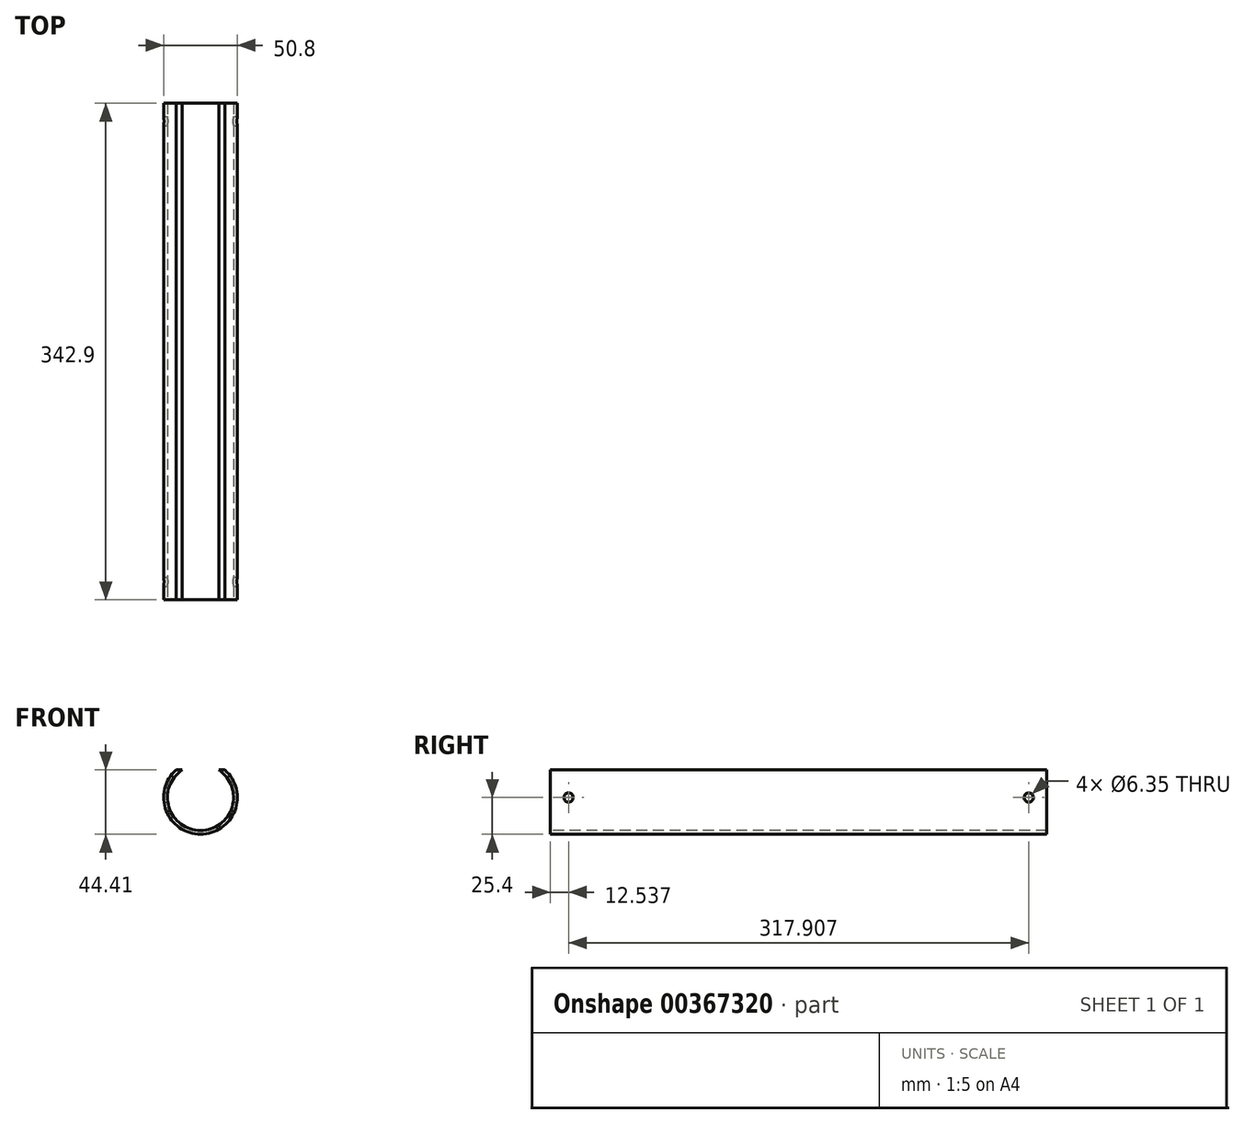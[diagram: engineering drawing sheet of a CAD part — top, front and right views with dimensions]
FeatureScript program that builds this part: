
annotation { "Feature Type Name" : "Feature", "Feature Type Description" : "" }
export const myFeature = defineFeature(function(context is Context, id is Id, definition is map)
    precondition{}
    {
        {
            var Q0;
            Q0=qCreatedBy(makeId("Front.planeOp"),FACE);
            var sketch = newSketch(context, id + "F0", { "sketchPlane" : qUnion([Q0])});
            skCircle(sketch, "E0", {"center": v(0, 0) * mm, "radius": 25.4 * mm});
            skSolve(sketch);
        }
        {
            var Q0;
            Q0 = qSketchRegion(id + "F0", true);
            extrude(context, id + "F1", {"entities" : qUnion([Q0]), "depth" : 342.9 * mm});
        }
        {
            var Q0;
            Q0=makeQuery(id+"F1.opExtrude","CAP_FACE",FACE,{"disambiguationData":[OSD([sQuery(id+"F0.wireOp",EDGE,"E0")])],"isStart":false});
            var sketch = newSketch(context, id + "F2", { "sketchPlane" : qUnion([Q0])});
            skCircle(sketch, "E1", {"center": v(0, 0) * mm, "radius": 22.86 * mm});
            skSolve(sketch);
        }
        {
            var Q0;
            Q0 = qSketchRegion(id + "F2", true);
            var Q1;
            Q1=makeQuery(id+"F1.opExtrude","CAP_FACE",FACE,{"disambiguationData":[OSD([sQuery(id+"F0.wireOp",EDGE,"E0")])],"isStart":true});
            extrude(context, id + "F3", {"entities" : qUnion([Q0]), "operationType" : NewBodyOperationType.REMOVE, "endBound" : BoundingType.UP_TO_SURFACE, "oppositeDirection" : true, "endBoundEntityFace" : qUnion([Q1]), "depth" : 25.4 * mm});
        }
        {
            var Q0;
            Q0=makeQuery(id+"F1.opExtrude","CAP_FACE",FACE,{"disambiguationData":[OSD([sQuery(id+"F0.wireOp",EDGE,"E0")])],"isStart":false});
            var sketch = newSketch(context, id + "F4", { "sketchPlane" : qUnion([Q0])});
            skPoint(sketch, "E2", {"position": v(-12.7, 19) * mm});
            skPoint(sketch, "E3", {"position": v(12.7, 19) * mm});
            skLineSegment(sketch, "E4", {"start": v(-12.7, 19) * mm, "end": v(16.85, 19) * mm});
            skLineSegment(sketch, "E5", {"start": v(-12.7, 19) * mm, "end": v(-16.85, 19) * mm});
            skSolve(sketch);
        }
        {
            var Q0;
            {var subQ5=sQuery(id+"F4.wireOp",EDGE,"E5");Q0=makeQuery(id+"F4.imprint","IMPRINT",FACE,{"disambiguationData":[TD([[makeQuery(id+"F4.imprint","IMPRINT",EDGE,{"derivedFrom":subQ5}),-1.0]])]});}
            var Q1;
            Q1=makeQuery(id+"F1.opExtrude","CAP_FACE",FACE,{"disambiguationData":[OSD([sQuery(id+"F0.wireOp",EDGE,"E0")])],"isStart":true});
            extrude(context, id + "F5", {"entities" : qUnion([Q0]), "operationType" : NewBodyOperationType.REMOVE, "endBound" : BoundingType.UP_TO_SURFACE, "oppositeDirection" : true, "endBoundEntityFace" : qUnion([Q1]), "depth" : 25.4 * mm});
        }
        {
            var Q0;
            Q0=qCreatedBy(makeId("Right.planeOp"),FACE);
            cPlane(context, id + "F6", {"entities" : qUnion([Q0]), "cplaneType" : CPlaneType.OFFSET, "offset" : 36.83 * mm, "width" : 152.4 * mm, "height" : 152.4 * mm});
        }
        {
            var Q0;
            Q0=qCreatedBy(id+"F6.planeOp",FACE);
            var sketch = newSketch(context, id + "F7", { "sketchPlane" : qUnion([Q0])});
            skCircle(sketch, "E6", {"center": v(-330.36, 0) * mm, "radius": 3.18 * mm});
            skCircle(sketch, "E7", {"center": v(-12.46, 0) * mm, "radius": 3.18 * mm});
            skSolve(sketch);
        }
        {
            var Q0;
            Q0 = qSketchRegion(id + "F7", true);
            extrude(context, id + "F8", {"entities" : qUnion([Q0]), "operationType" : NewBodyOperationType.REMOVE, "endBound" : BoundingType.THROUGH_ALL, "oppositeDirection" : true, "depth" : 25.4 * mm});
        }
    });
